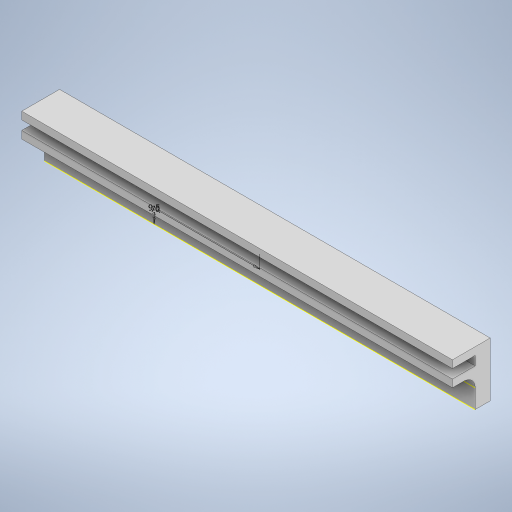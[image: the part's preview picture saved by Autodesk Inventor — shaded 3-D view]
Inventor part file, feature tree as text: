
AUTODESK INVENTOR PART (.ipt)
format: ipt  version: 2023 (Build 270158000, 158)  size: 290,816 bytes
history: native  units: in
note: dims shown in document units (in); Inventor stores cm internally (conversion verified against a paired STEP export)
features: extrude x3, hole x3, sketch x3, fillet x1
ambient origin geometry x8: Origin, YZ Plane, XZ Plane, XY Plane, X Axis, Y Axis, Z Axis, Center Point
bodies: Solid1 (feature_tree)
feature tree (10):
  extrude  "Extrusion1"  Depth=1.4173in
  extrude  "Extrusion2"  Depth=0.1969in
  extrude  "Extrusion3"  Depth=0.1969in
  fillet  "Fillet1"  Radius=0.5906in
  hole  "Hole1"  [1 undecoded]
  hole  "Hole2"  [1 undecoded]
  hole  "Hole3"  [1 undecoded]
  sketch  "Sketch1"  dims[d0=11.2205in d1=1.4173in]
  sketch  "Sketch4"  dims[d2=0.3937in d3=0.0in d4=0.1969in]
  sketch  "Sketch5"  dims[d5=11.2205in d6=0.1969in d7=0.5906in d8=0.0in d9=11.2205in d10=0.1969in d11=0.5906in d12=0.0in d13=0.2953in d15=0.1969in d16=0.2362in d17=0.1575in d18=0.0787in d19=90.0deg d20=0.315in d21=0.8108in d23=0.1969in d24=0.1969in d25=0.2362in d26=0.1575in d27=0.0787in d28=90.0deg d29=0.315in d30=0.8108in d31=0.1969in d32=0.1969in d33=0.2362in d34=0.1575in d35=0.0787in d36=90.0deg d37=0.315in d38=0.8108in d39=2.7559in d43=0.374in d47=0.4331in d48=0.2756in d50=2.7559in d51=0.374in d14=0.0in]
note: 3 required parameter values undecoded (feature->parameter linkage not recoverable at this tier; creation-order binding heuristic only, values carry confidence <= 0.55)
